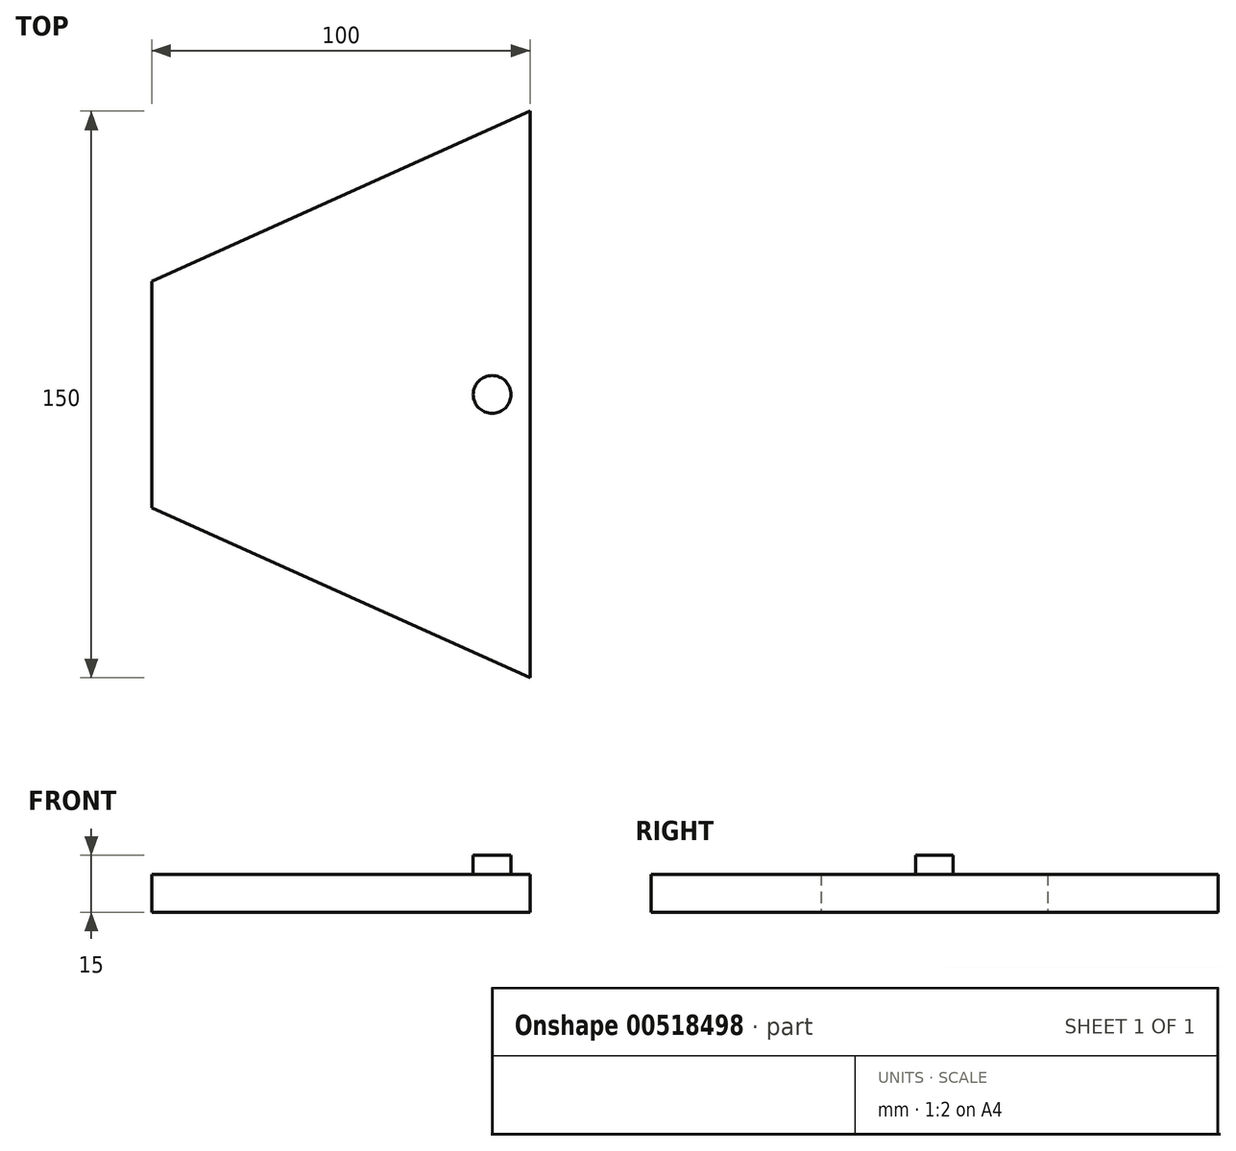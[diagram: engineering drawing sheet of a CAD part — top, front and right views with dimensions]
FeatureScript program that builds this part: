
annotation { "Feature Type Name" : "Feature", "Feature Type Description" : "" }
export const myFeature = defineFeature(function(context is Context, id is Id, definition is map)
    precondition{}
    {
        {
            var Q0;
            Q0=qCreatedBy(makeId("Top.planeOp"),FACE);
            var sketch = newSketch(context, id + "F0", { "sketchPlane" : qUnion([Q0])});
            skLineSegment(sketch, "E0", {"start": v(0, -30) * mm, "end": v(0, 30) * mm});
            skLineSegment(sketch, "E1", {"start": v(0, 30) * mm, "end": v(100, 75) * mm});
            skLineSegment(sketch, "E2", {"start": v(100, 75) * mm, "end": v(100, -75) * mm});
            skLineSegment(sketch, "E3", {"start": v(100, -75) * mm, "end": v(0, -30) * mm});
            skSolve(sketch);
        }
        {
            var Q0;
            Q0=makeQuery(id+"F0.imprint","IMPRINT",FACE,{"disambiguationData":[TD([[makeQuery(id+"F0.imprint","IMPRINT",EDGE,{"derivedFrom":sQuery(id+"F0.wireOp",EDGE,"E0")}),-1.0]])]});
            extrude(context, id + "F1", {"entities" : qUnion([Q0]), "depth" : 10 * mm, "offsetDistance" : 25 * mm});
        }
        {
            var Q0;
            Q0=makeQuery(id+"F1.opExtrude","CAP_FACE",FACE,{"disambiguationData":[OSD([sQuery(id+"F0.wireOp",EDGE,"E0"),sQuery(id+"F0.wireOp",EDGE,"E1"),sQuery(id+"F0.wireOp",EDGE,"E2"),sQuery(id+"F0.wireOp",EDGE,"E3")])],"isStart":false});
            var sketch = newSketch(context, id + "F2", { "sketchPlane" : qUnion([Q0])});
            skCircle(sketch, "E4", {"center": v(90, 0) * mm, "radius": 5 * mm});
            skSolve(sketch);
        }
        {
            var Q0;
            Q0 = qSketchRegion(id + "F2", true);
            extrude(context, id + "F3", {"entities" : qUnion([Q0]), "operationType" : NewBodyOperationType.ADD, "depth" : 5 * mm, "offsetDistance" : 25 * mm});
        }
    });
